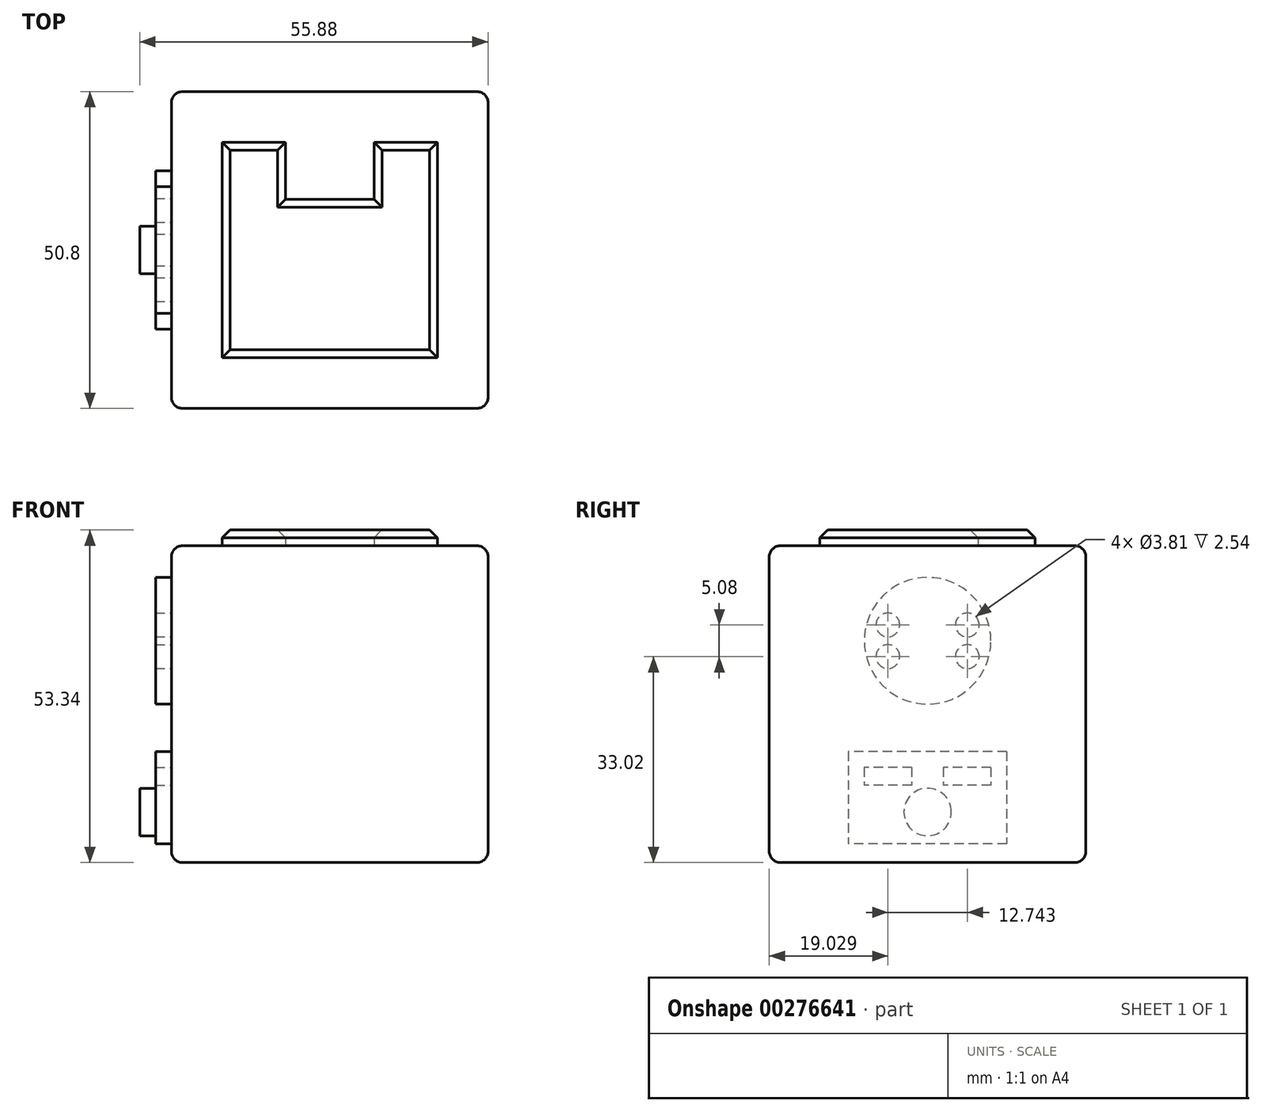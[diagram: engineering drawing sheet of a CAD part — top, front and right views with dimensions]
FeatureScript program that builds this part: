
annotation { "Feature Type Name" : "Feature", "Feature Type Description" : "" }
export const myFeature = defineFeature(function(context is Context, id is Id, definition is map)
    precondition{}
    {
        {
            var Q0;
            Q0=qCreatedBy(makeId("Front.planeOp"),FACE);
            var sketch = newSketch(context, id + "F0", { "sketchPlane" : qUnion([Q0])});
            skLineSegment(sketch, "E0.bottom", {"start": v(0, 0) * mm, "end": v(50.8, 0) * mm});
            skLineSegment(sketch, "E0.top", {"start": v(0, 50.8) * mm, "end": v(50.8, 50.8) * mm});
            skLineSegment(sketch, "E0.left", {"start": v(0, 0) * mm, "end": v(0, 50.8) * mm});
            skLineSegment(sketch, "E0.right", {"start": v(50.8, 0) * mm, "end": v(50.8, 50.8) * mm});
            skSolve(sketch);
        }
        {
            var Q0;
            Q0 = qSketchRegion(id + "F0", true);
            extrude(context, id + "F1", {"entities" : qUnion([Q0]), "depth" : 50.8 * mm});
        }
        {
            var Q0;
            Q0=qCreatedBy(makeId("Right.planeOp"),FACE);
            var sketch = newSketch(context, id + "F2", { "sketchPlane" : qUnion([Q0])});
            skCircle(sketch, "E1", {"center": v(-25.4, 35.56) * mm, "radius": 10.16 * mm});
            skLineSegment(sketch, "E2", {"start": v(-25.4, 35.56) * mm, "end": v(0, 35.56) * mm, "construction": true});
            skLineSegment(sketch, "E3", {"start": v(-25.4, 35.56) * mm, "end": v(-25.4, 50.8) * mm, "construction": true});
            skSolve(sketch);
        }
        {
            var Q0;
            Q0 = qSketchRegion(id + "F2", true);
            extrude(context, id + "F3", {"entities" : qUnion([Q0]), "operationType" : NewBodyOperationType.ADD, "oppositeDirection" : true, "depth" : 2.54 * mm});
        }
        {
            var Q0;
            Q0=qCreatedBy(makeId("Right.planeOp"),FACE);
            var sketch = newSketch(context, id + "F4", { "sketchPlane" : qUnion([Q0])});
            skLineSegment(sketch, "E4.bottom", {"start": v(-12.7, 17.78) * mm, "end": v(-38.1, 17.78) * mm});
            skLineSegment(sketch, "E4.top", {"start": v(-12.7, 3.02) * mm, "end": v(-38.1, 3.02) * mm});
            skLineSegment(sketch, "E4.left", {"start": v(-12.7, 17.78) * mm, "end": v(-12.7, 3.02) * mm});
            skLineSegment(sketch, "E4.right", {"start": v(-38.1, 17.78) * mm, "end": v(-38.1, 3.02) * mm});
            skSolve(sketch);
        }
        {
            var Q0;
            Q0 = qSketchRegion(id + "F4", true);
            extrude(context, id + "F5", {"entities" : qUnion([Q0]), "operationType" : NewBodyOperationType.ADD, "oppositeDirection" : true, "depth" : 2.54 * mm});
        }
        {
            var Q0;
            Q0=qCreatedBy(makeId("Right.planeOp"),FACE);
            var sketch = newSketch(context, id + "F6", { "sketchPlane" : qUnion([Q0])});
            skLineSegment(sketch, "E5.bottom", {"start": v(-15.24, 15.24) * mm, "end": v(-22.86, 15.24) * mm});
            skLineSegment(sketch, "E5.top", {"start": v(-15.24, 12.36) * mm, "end": v(-22.86, 12.36) * mm});
            skLineSegment(sketch, "E5.left", {"start": v(-15.24, 15.24) * mm, "end": v(-15.24, 12.36) * mm});
            skLineSegment(sketch, "E5.right", {"start": v(-22.86, 15.24) * mm, "end": v(-22.86, 12.36) * mm});
            skLineSegment(sketch, "E6.bottom", {"start": v(-27.94, 15.24) * mm, "end": v(-35.56, 15.24) * mm});
            skLineSegment(sketch, "E6.top", {"start": v(-27.94, 12.36) * mm, "end": v(-35.56, 12.36) * mm});
            skLineSegment(sketch, "E6.left", {"start": v(-27.94, 15.24) * mm, "end": v(-27.94, 12.36) * mm});
            skLineSegment(sketch, "E6.right", {"start": v(-35.56, 15.24) * mm, "end": v(-35.56, 12.36) * mm});
            skSolve(sketch);
        }
        {
            var Q0;
            Q0 = qSketchRegion(id + "F6", true);
            extrude(context, id + "F7", {"entities" : qUnion([Q0]), "operationType" : NewBodyOperationType.REMOVE, "oppositeDirection" : true, "depth" : 5.08 * mm});
        }
        {
            var Q0;
            Q0=qCreatedBy(makeId("Right.planeOp"),FACE);
            var sketch = newSketch(context, id + "F8", { "sketchPlane" : qUnion([Q0])});
            skCircle(sketch, "E7", {"center": v(-25.4, 8.1) * mm, "radius": 3.81 * mm});
            skLineSegment(sketch, "E8", {"start": v(-25.4, 22.5) * mm, "end": v(-25.4, -5.44) * mm, "construction": true});
            skSolve(sketch);
        }
        {
            var Q0;
            Q0 = qSketchRegion(id + "F8", true);
            extrude(context, id + "F9", {"entities" : qUnion([Q0]), "operationType" : NewBodyOperationType.ADD, "oppositeDirection" : true, "depth" : 5.08 * mm});
        }
        {
            var Q0;
            Q0=qCreatedBy(makeId("Right.planeOp"),FACE);
            var sketch = newSketch(context, id + "F10", { "sketchPlane" : qUnion([Q0])});
            skCircle(sketch, "E9", {"center": v(-31.77, 38.1) * mm, "radius": 1.9 * mm});
            skLineSegment(sketch, "E10", {"start": v(-25.4, 51.57) * mm, "end": v(-25.4, 16.67) * mm, "construction": true});
            skLineSegment(sketch, "E11", {"start": v(-6.73, 35.56) * mm, "end": v(-45.88, 35.56) * mm, "construction": true});
            skCircle(sketch, "E12.MirrorC", {"center": v(-19.03, 38.1) * mm, "radius": 1.9 * mm});
            skLineSegment(sketch, "E13.MirrorCS", {"start": v(-44.07, 35.56) * mm, "end": v(-4.92, 35.56) * mm, "construction": true});
            skCircle(sketch, "E14.MirrorC", {"center": v(-19.03, 33.02) * mm, "radius": 1.9 * mm});
            skCircle(sketch, "E15.MirrorC", {"center": v(-31.77, 33.02) * mm, "radius": 1.9 * mm});
            skSolve(sketch);
        }
        {
            var Q0;
            Q0 = qSketchRegion(id + "F10", true);
            extrude(context, id + "F11", {"entities" : qUnion([Q0]), "operationType" : NewBodyOperationType.REMOVE, "oppositeDirection" : true, "depth" : 20.32 * mm});
        }
        {
            var Q0;
            Q0=makeQuery(id+"F1.opExtrude","CAP_FACE",FACE,{"disambiguationData":[OSD([sQuery(id+"F0.wireOp",EDGE,"E0.bottom"),sQuery(id+"F0.wireOp",EDGE,"E0.top"),sQuery(id+"F0.wireOp",EDGE,"E0.left"),sQuery(id+"F0.wireOp",EDGE,"E0.right")])],"isStart":false});
            var Q1;
            Q1=makeQuery(id+"F1.opExtrude","SWEPT_FACE",FACE,{"disambiguationData":[OSD([sQuery(id+"F0.wireOp",EDGE,"E0.top")])]});
            var Q2;
            Q2=makeQuery(id+"F1.opExtrude","SWEPT_FACE",FACE,{"disambiguationData":[OSD([sQuery(id+"F0.wireOp",EDGE,"E0.right")])]});
            var Q3;
            Q3=makeQuery(id+"F1.opExtrude","CAP_FACE",FACE,{"disambiguationData":[OSD([sQuery(id+"F0.wireOp",EDGE,"E0.bottom"),sQuery(id+"F0.wireOp",EDGE,"E0.top"),sQuery(id+"F0.wireOp",EDGE,"E0.left"),sQuery(id+"F0.wireOp",EDGE,"E0.right")])],"isStart":true});
            var Q4;
            Q4=makeQuery(id+"F1.opExtrude","SWEPT_FACE",FACE,{"disambiguationData":[OSD([sQuery(id+"F0.wireOp",EDGE,"E0.bottom")])]});
            fillet(context, id + "F12", {"entities" : qUnion([Q0, Q1, Q2, Q3, Q4]), "radius" : 1.78 * mm, "tangentPropagation" : true, "allowEdgeOverflow" : false});
        }
        {
            var Q0;
            Q0=qCreatedBy(makeId("Top.planeOp"),FACE);
            var sketch = newSketch(context, id + "F13", { "sketchPlane" : qUnion([Q0])});
            skLineSegment(sketch, "E16.bottom", {"start": v(8.13, -8.13) * mm, "end": v(18.29, -8.13) * mm});
            skLineSegment(sketch, "E16.top", {"start": v(8.13, -42.67) * mm, "end": v(42.67, -42.67) * mm});
            skLineSegment(sketch, "E16.left", {"start": v(8.13, -8.13) * mm, "end": v(8.13, -42.67) * mm});
            skLineSegment(sketch, "E16.right", {"start": v(42.67, -8.13) * mm, "end": v(42.67, -42.67) * mm});
            skLineSegment(sketch, "E17.trimOffspring", {"start": v(32.51, -8.13) * mm, "end": v(42.67, -8.13) * mm});
            skLineSegment(sketch, "E18", {"start": v(18.29, -8.13) * mm, "end": v(18.29, -17.27) * mm});
            skLineSegment(sketch, "E19", {"start": v(18.29, -17.27) * mm, "end": v(32.51, -17.27) * mm});
            skLineSegment(sketch, "E20", {"start": v(32.51, -17.27) * mm, "end": v(32.51, -8.13) * mm});
            skSolve(sketch);
        }
        {
            var Q0;
            Q0 = qSketchRegion(id + "F13", true);
            extrude(context, id + "F14", {"entities" : qUnion([Q0]), "operationType" : NewBodyOperationType.ADD, "depth" : 53.34 * mm});
        }
        {
            var Q0;
            Q0=makeQuery(id+"F14.opExtrude","CAP_FACE",FACE,{"disambiguationData":[OSD([sQuery(id+"F13.wireOp",EDGE,"E16.bottom"),sQuery(id+"F13.wireOp",EDGE,"E16.top"),sQuery(id+"F13.wireOp",EDGE,"E16.left"),sQuery(id+"F13.wireOp",EDGE,"E16.right"),sQuery(id+"F13.wireOp",EDGE,"E17.trimOffspring"),sQuery(id+"F13.wireOp",EDGE,"E18"),sQuery(id+"F13.wireOp",EDGE,"E19"),sQuery(id+"F13.wireOp",EDGE,"E20")])],"isStart":false});
            chamfer(context, id + "F15", {"entities" : qUnion([Q0]), "width" : 1.27 * mm, "tangentPropagation" : true});
        }
    });
